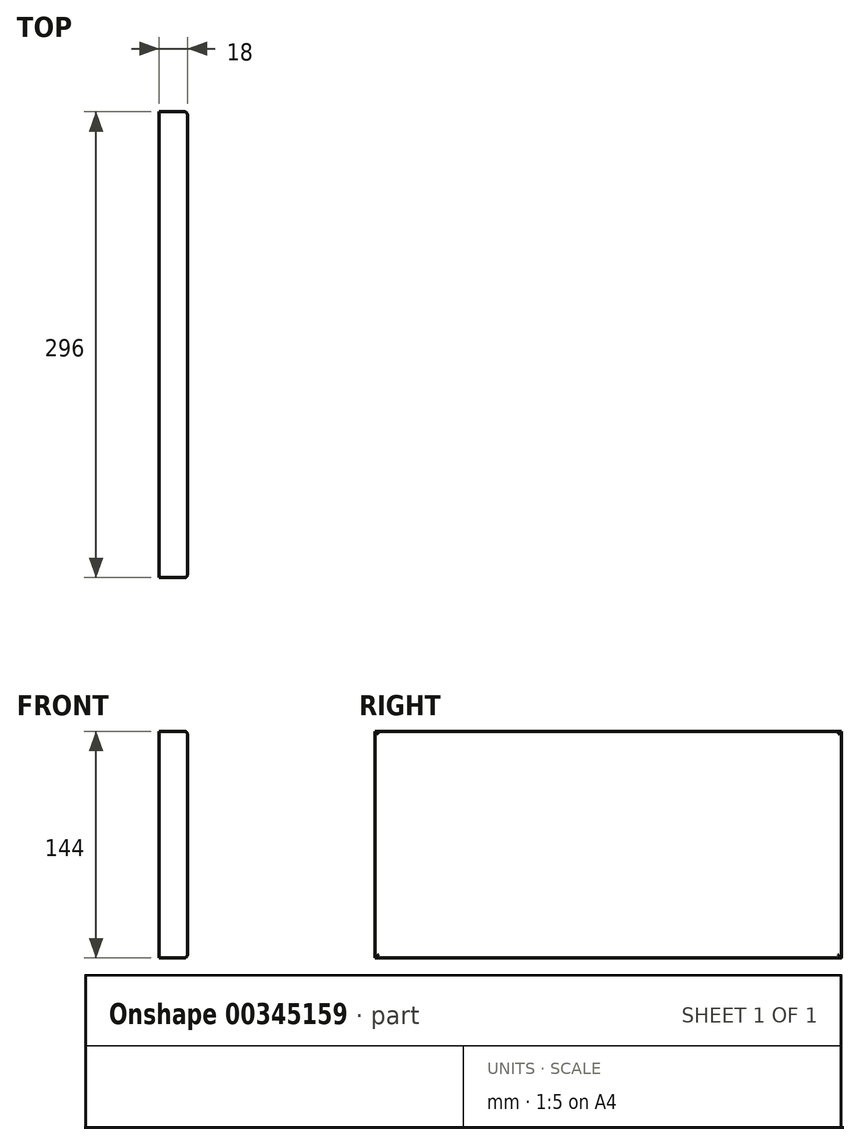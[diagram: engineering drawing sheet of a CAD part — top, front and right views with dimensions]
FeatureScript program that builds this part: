
annotation { "Feature Type Name" : "Feature", "Feature Type Description" : "" }
export const myFeature = defineFeature(function(context is Context, id is Id, definition is map)
    precondition{}
    {
        {
            var Q0;
            Q0=qCreatedBy(makeId("Right.planeOp"),FACE);
            var sketch = newSketch(context, id + "F0", { "sketchPlane" : qUnion([Q0])});
            skLineSegment(sketch, "E0.bottom", {"start": v(0, 0) * mm, "end": v(-43.04, 0) * mm});
            skLineSegment(sketch, "E0.top", {"start": v(0, 34.48) * mm, "end": v(-43.04, 34.48) * mm});
            skLineSegment(sketch, "E0.left", {"start": v(0, 0) * mm, "end": v(0, 34.48) * mm});
            skLineSegment(sketch, "E0.right", {"start": v(-43.04, 0) * mm, "end": v(-43.04, 34.48) * mm});
            skSolve(sketch);
        }
        {
            var Q0;
            Q0=makeQuery(id+"F0.imprint","IMPRINT",FACE,{"disambiguationData":[TD([[makeQuery(id+"F0.imprint","IMPRINT",EDGE,{"derivedFrom":sQuery(id+"F0.wireOp",EDGE,"E0.bottom")}),-1.0]])]});
            extrude(context, id + "F1", {"entities" : qUnion([Q0]), "oppositeDirection" : true, "depth" : 25 * mm});
        }
        {
            var Q0;
            Q0=makeQuery(id+"F1.opExtrude","SWEPT_FACE",FACE,{"disambiguationData":[OSD([sQuery(id+"F0.wireOp",EDGE,"E0.bottom")])]});
            extrude(context, id + "F2", {"entities" : qUnion([Q0]), "operationType" : NewBodyOperationType.ADD, "oppositeDirection" : true, "depth" : 144 * mm});
        }
        {
            var Q0;
            {var subQ0=sQuery(id+"F0.wireOp",EDGE,"E0.bottom");Q0=makeQuery(id+"F2.boolean.opBoolean","MERGE",FACE,{"derivedFrom":[makeQuery(id+"F1.opExtrude","CAP_FACE",FACE,{"disambiguationData":[OSD([subQ0,sQuery(id+"F0.wireOp",EDGE,"E0.top"),sQuery(id+"F0.wireOp",EDGE,"E0.left"),sQuery(id+"F0.wireOp",EDGE,"E0.right")])],"isStart":true}),makeQuery(id+"F2.opExtrude","SWEPT_FACE",FACE,{"disambiguationData":[OSD([subQ0]),TDD([makeQuery(id+"F1.opExtrude","CAP_EDGE",EDGE,{"disambiguationData":[OSD([subQ0])],"isStart":true})])]})]});}
            extrude(context, id + "F3", {"entities" : qUnion([Q0]), "operationType" : NewBodyOperationType.INTERSECT, "oppositeDirection" : true, "depth" : 18 * mm});
        }
        {
            var Q0;
            {var subQ0=sQuery(id+"F0.wireOp",EDGE,"E0.left");Q0=makeQuery(id+"F2.boolean.opBoolean","MERGE",FACE,{"derivedFrom":[makeQuery(id+"F1.opExtrude","SWEPT_FACE",FACE,{"disambiguationData":[OSD([subQ0])]}),makeQuery(id+"F2.opExtrude","SWEPT_FACE",FACE,{"disambiguationData":[OSD([sQuery(id+"F0.wireOp",EDGE,"E0.bottom"),subQ0])]})]});}
            extrude(context, id + "F4", {"entities" : qUnion([Q0]), "operationType" : NewBodyOperationType.ADD, "oppositeDirection" : true, "depth" : 296 * mm});
        }
        {
            var Q0;
            {var subQ0=sQuery(id+"F0.wireOp",EDGE,"E0.left");var subQ1=sQuery(id+"F0.wireOp",EDGE,"E0.bottom");Q0=makeQuery(id+"F4.boolean.opBoolean","MERGE",FACE,{"derivedFrom":[makeQuery(id+"F2.boolean.opBoolean","MERGE",FACE,{"derivedFrom":[makeQuery(id+"F1.opExtrude","CAP_FACE",FACE,{"disambiguationData":[OSD([subQ1,sQuery(id+"F0.wireOp",EDGE,"E0.top"),subQ0,sQuery(id+"F0.wireOp",EDGE,"E0.right")])],"isStart":true}),makeQuery(id+"F2.opExtrude","SWEPT_FACE",FACE,{"disambiguationData":[OSD([subQ1]),TDD([makeQuery(id+"F1.opExtrude","CAP_EDGE",EDGE,{"disambiguationData":[OSD([subQ1])],"isStart":true})])]})]}),makeQuery(id+"F4.opExtrude","SWEPT_FACE",FACE,{"disambiguationData":[OSD([subQ1,subQ0]),TDD([makeQuery(id+"F2.boolean.opBoolean","MERGE",EDGE,{"derivedFrom":[makeQuery(id+"F1.opExtrude","CAP_EDGE",EDGE,{"disambiguationData":[OSD([subQ0])],"isStart":true}),makeQuery(id+"F2.opExtrude","SWEPT_EDGE",EDGE,{"disambiguationData":[OSD([subQ1,subQ0]),TDD([makeQuery(id+"F1.opExtrude","CAP_VERTEX",VERTEX,{"disambiguationData":[OSD([subQ1,subQ0])],"isStart":true})])]})]})])]})]});}
            fillet(context, id + "F5", {"entities" : qUnion([Q0]), "radius" : 2 * mm, "tangentPropagation" : true, "allowEdgeOverflow" : false});
        }
    });
